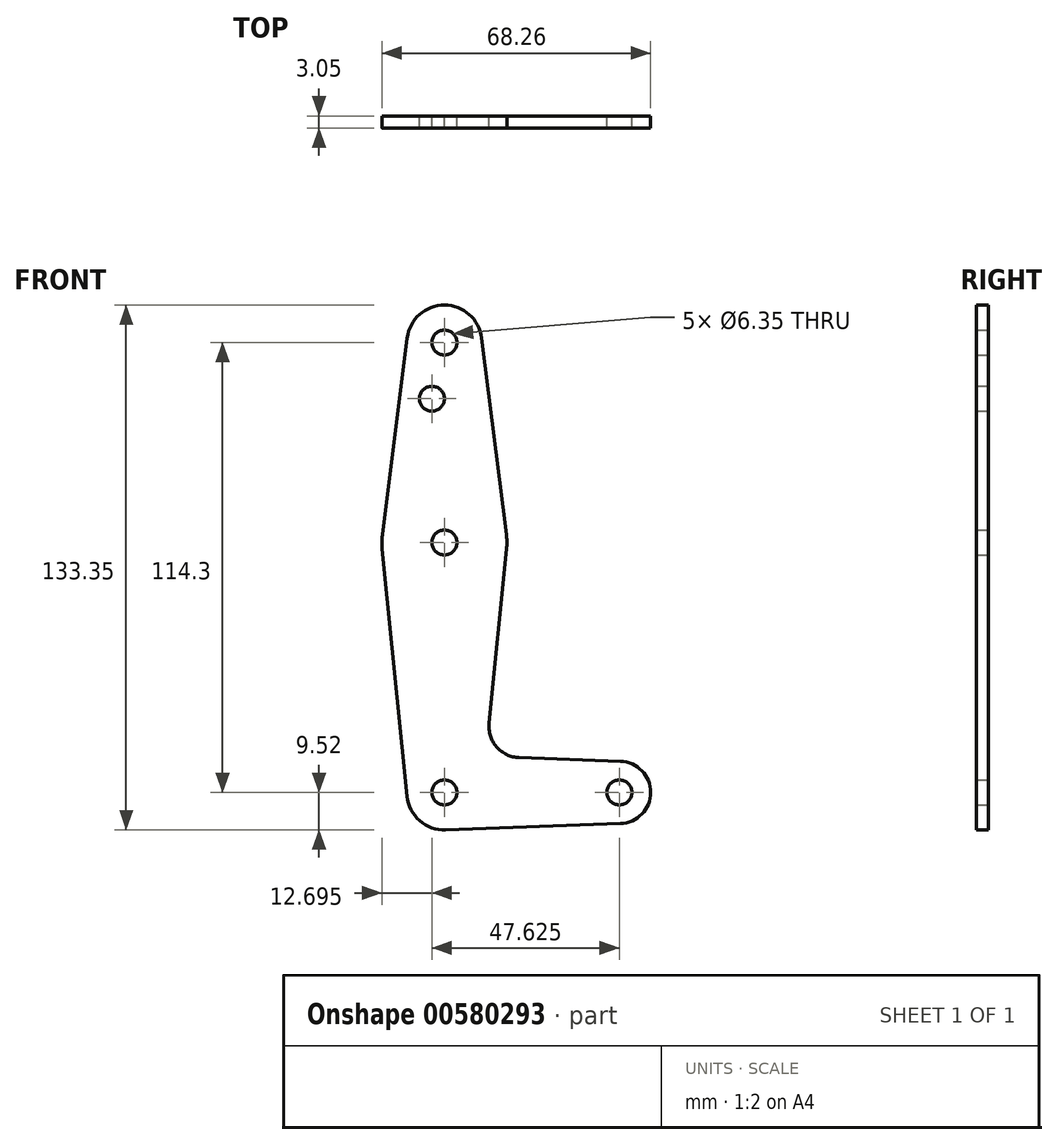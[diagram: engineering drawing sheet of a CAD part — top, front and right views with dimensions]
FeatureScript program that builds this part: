
annotation { "Feature Type Name" : "Feature", "Feature Type Description" : "" }
export const myFeature = defineFeature(function(context is Context, id is Id, definition is map)
    precondition{}
    {
        {
            var Q0;
            Q0=qCreatedBy(makeId("Front.planeOp"),FACE);
            var sketch = newSketch(context, id + "F0", { "sketchPlane" : qUnion([Q0])});
            skLineSegment(sketch, "E0", {"start": v(0, 114.3) * mm, "end": v(0, 63.5) * mm, "construction": true});
            skLineSegment(sketch, "E1", {"start": v(0, 63.5) * mm, "end": v(0, 0) * mm, "construction": true});
            skLineSegment(sketch, "E2", {"start": v(0, 0) * mm, "end": v(44.45, 0) * mm, "construction": true});
            skCircle(sketch, "E3", {"center": v(0, 114.3) * mm, "radius": 9.53 * mm});
            skCircle(sketch, "E4", {"center": v(0, 63.5) * mm, "radius": 15.88 * mm});
            skCircle(sketch, "E5", {"center": v(44.45, 0) * mm, "radius": 7.94 * mm});
            skCircle(sketch, "E6", {"center": v(0, 0) * mm, "radius": 9.53 * mm});
            skLineSegment(sketch, "E7", {"start": v(-9.45, 115.5) * mm, "end": v(-15.75, 65.48) * mm});
            skLineSegment(sketch, "E8", {"start": v(9.45, 115.5) * mm, "end": v(15.75, 65.48) * mm});
            skLineSegment(sketch, "E9", {"start": v(-15.8, 61.91) * mm, "end": v(-9.48, -0.95) * mm});
            skLineSegment(sketch, "E10", {"start": v(15.8, 61.91) * mm, "end": v(11.34, 17.6) * mm});
            skLineSegment(sketch, "E11", {"start": v(18.97, 8.85) * mm, "end": v(44.73, 7.93) * mm});
            skLineSegment(sketch, "E12", {"start": v(0.34, -9.52) * mm, "end": v(44.73, -7.93) * mm});
            skCircle(sketch, "E13", {"center": v(0, 114.3) * mm, "radius": 3.18 * mm});
            skCircle(sketch, "E14", {"center": v(0, 0) * mm, "radius": 3.18 * mm});
            skCircle(sketch, "E15", {"center": v(0, 63.5) * mm, "radius": 3.18 * mm});
            skCircle(sketch, "E16", {"center": v(44.45, 0) * mm, "radius": 3.18 * mm});
            skCircle(sketch, "E17", {"center": v(-3.17, 100.03) * mm, "radius": 3.18 * mm});
            skArc(sketch, "E18", {"start": v(11.34, 17.6) * mm, "mid": v(13.26, 11.57) * mm, "end": v(18.97, 8.85) * mm});
            skLineSegment(sketch, "E19.trimOffspring", {"start": v(9.57, 0) * mm, "end": v(9.48, -0.95) * mm});
            skSolve(sketch);
        }
        {
            var Q0;
            Q0 = qSketchRegion(id + "F0", true);
            extrude(context, id + "F1", {"entities" : qUnion([Q0]), "depth" : 3.05 * mm, "offsetDistance" : 25.4 * mm});
        }
    });
